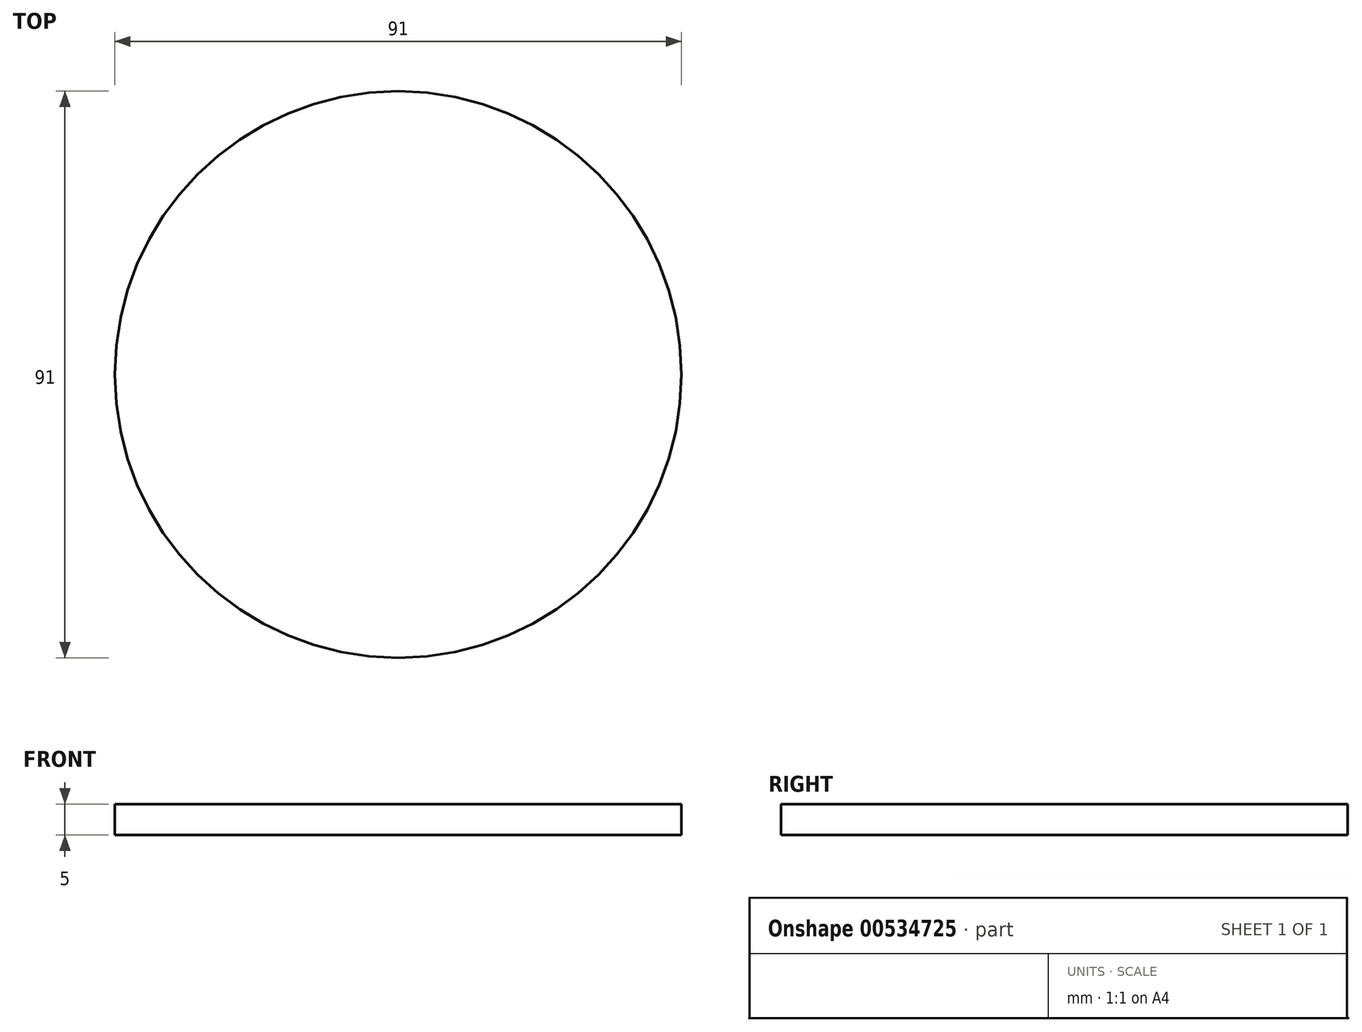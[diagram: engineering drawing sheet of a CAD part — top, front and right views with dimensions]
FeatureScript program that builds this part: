
annotation { "Feature Type Name" : "Feature", "Feature Type Description" : "" }
export const myFeature = defineFeature(function(context is Context, id is Id, definition is map)
    precondition{}
    {
        {
            var Q0;
            Q0=qCreatedBy(makeId("Top.planeOp"),FACE);
            var sketch = newSketch(context, id + "F0", { "sketchPlane" : qUnion([Q0])});
            skCircle(sketch, "E0", {"center": v(-46.3, 17.12) * mm, "radius": 45.5 * mm});
            skCircle(sketch, "E1", {"center": v(-46.3, 17.12) * mm, "radius": 45 * mm});
            skSolve(sketch);
        }
        {
            var Q0;
            Q0=sQuery(id+"F0.wireOp",EDGE,"E1");
            var Q1;
            Q1=sQuery(id+"F0.wireOp",EDGE,"E0");
            extrude(context, id + "F1", {"bodyType" : ToolBodyType.SURFACE, "surfaceEntities" : qUnion([Q0, Q1]), "depth" : 80 * mm, "offsetDistance" : 25 * mm});
        }
        {
            var Q0;
            Q0=qCreatedBy(makeId("Top.planeOp"),FACE);
            var sketch = newSketch(context, id + "F2", { "sketchPlane" : qUnion([Q0])});
            skCircle(sketch, "E2", {"center": v(-46.3, 17.12) * mm, "radius": 45.5 * mm});
            skSolve(sketch);
        }
        {
            var Q0;
            Q0=qSketchRegion(id+"F2",true);
            extrude(context, id + "F3", {"entities" : qUnion([Q0]), "depth" : 5 * mm, "offsetDistance" : 25 * mm});
        }
    });
